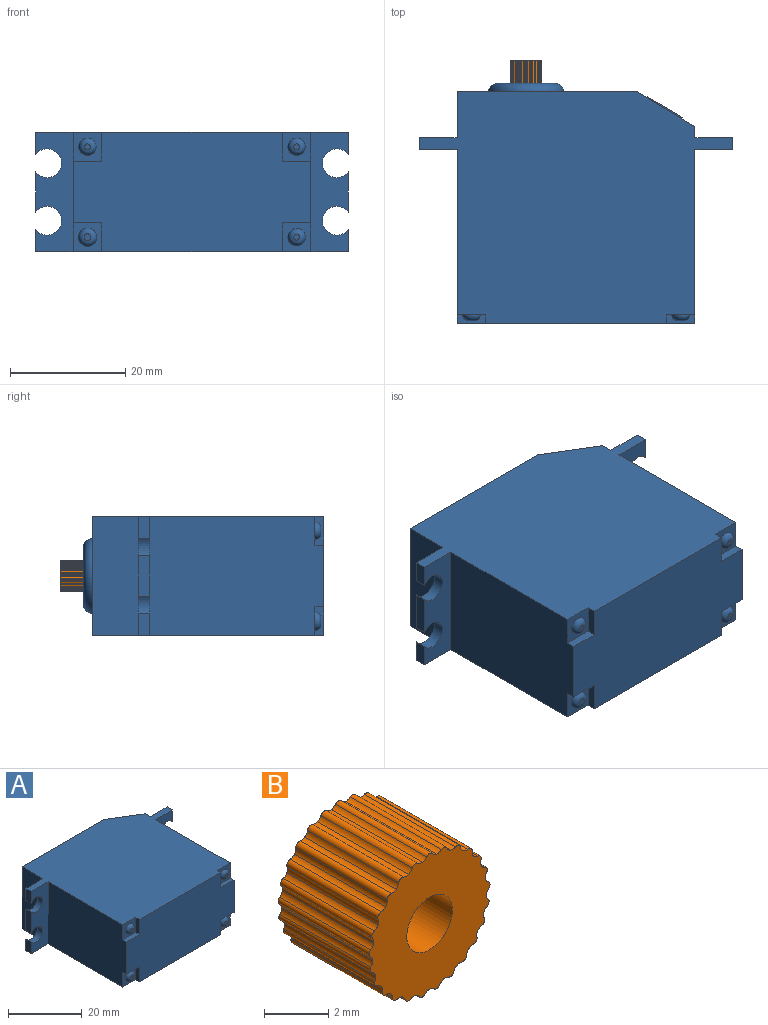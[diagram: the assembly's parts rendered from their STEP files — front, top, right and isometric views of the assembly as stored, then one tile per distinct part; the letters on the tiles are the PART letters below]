
ASSEMBLY  parts=2 mates=1
PART A: 52 faces, bbox 54.3x41.7x20.7 mm
  f0: plane 20.7x10mm, normal (0.51,0.86,0), area 143.4mm2, adj f6,f9,f11,f12,f43,f44,f45,f46
  f1: plane 7x2mm, normal (1,0,0), area 14mm2, adj f34,f35,f39,f42
  f2: plane 7x2mm, normal (-1,0,0), area 14mm2, adj f36,f37,f40,f41
  f3: plane 3.85x2mm, normal (-1,0,0), area 7.7mm2, adj f11,f36,f37,f40
  f4: plane 3.85x2mm, normal (1,0,0), area 7.7mm2, adj f11,f34,f35,f39
  f5: plane 20.7x8mm, normal (-1,0,0), area 165.6mm2, adj f9,f11,f12,f36
  f6: plane 20.7x2mm, normal (1,0,0), area 41.4mm2, adj f0,f9,f11,f35
  f7: plane 41.3x20.7mm, normal (0,-1,0), area 754.9mm2, adj f8,f9,f10,f11,f13,f14,f16,f17
  f8: plane 30.2x20.7mm, normal (-1,0,0), area 610.1mm2, adj f7,f9,f11,f19,f21,f22,f24,f37
  f9: plane 54.3x40.2mm, normal (0,0,1), area 1641.3mm2, adj f0,f5,f6,f7,f8,f10,f12,f16
  f10: plane 30.2x20.7mm, normal (1,0,0), area 610.1mm2, adj f7,f9,f11,f14,f15,f17,f18,f34
  f11: plane 54.3x40.2mm, normal (0,0,-1), area 1641.3mm2, adj f0,f3,f4,f5,f6,f7,f8,f10
  f12: plane 31.3x20.7mm, normal (0,1,0), area 515.2mm2, adj f0,f5,f9,f11,f49
  f13: plane 5x1.5mm, normal (1,0,0), area 7.5mm2, adj f7,f11,f14,f15
  f14: plane 5x1.5mm, normal (0,0,-1), area 7.5mm2, adj f7,f10,f13,f15
  f15: plane 5x5mm, normal (0,-1,0), area 17.9mm2, adj f10,f11,f13,f14,f29
  f16: plane 5x1.5mm, normal (1,0,0), area 7.5mm2, adj f7,f9,f17,f18
  f17: plane 5x1.5mm, normal (0,0,1), area 7.5mm2, adj f7,f10,f16,f18
  f18: plane 5x5mm, normal (0,-1,0), area 17.9mm2, adj f9,f10,f16,f17,f30
  f19: plane 5x1.5mm, normal (0,0,1), area 7.5mm2, adj f7,f8,f20,f21
  f20: plane 5x1.5mm, normal (-1,0,0), area 7.5mm2, adj f7,f9,f19,f21
  f21: plane 5x5mm, normal (0,-1,0), area 17.9mm2, adj f8,f9,f19,f20,f31
  f22: plane 5x1.5mm, normal (0,0,-1), area 7.5mm2, adj f7,f8,f23,f24
  f23: plane 5x1.5mm, normal (-1,0,0), area 7.5mm2, adj f7,f11,f22,f24
  f24: plane 5x5mm, normal (0,-1,0), area 17.1mm2, adj f8,f11,f22,f23,f32
  f25: plane 1.18x1.18mm, normal (0,-1,0), area 1.1mm2, adj f32
  f26: plane 1x1mm, normal (0,-1,0), area 0.8mm2, adj f31
  f27: plane 1x1mm, normal (0,-1,0), area 0.8mm2, adj f30
  f28: plane 1x1mm, normal (0,-1,0), area 0.8mm2, adj f29
  f29: torus R=0.5mm, axis (0,-1,0), area 11.2mm2, adj f15,f28
  f30: torus R=0.5mm, axis (0,-1,0), area 11.2mm2, adj f18,f27
  f31: torus R=0.5mm, axis (0,-1,0), area 11.2mm2, adj f21,f26
  f32: torus R=0.59mm, axis (0,-1,0), area 12.1mm2, adj f24,f25
  f33: plane 3.85x2mm, normal (1,0,0), area 7.7mm2, adj f9,f34,f35,f42
  f34: plane 20.7x6.5mm, normal (0,-1,0), area 97.3mm2, adj f1,f4,f9,f10,f11,f33,f39,f42
  f35: plane 20.7x6.5mm, normal (0,1,0), area 97.3mm2, adj f1,f4,f6,f9,f11,f33,f39,f42
  f36: plane 20.7x6.5mm, normal (0,1,0), area 97.3mm2, adj f2,f3,f5,f9,f11,f38,f40,f41
  f37: plane 20.7x6.5mm, normal (0,-1,0), area 97.3mm2, adj f2,f3,f8,f9,f11,f38,f40,f41
  f38: plane 3.85x2mm, normal (-1,0,0), area 7.7mm2, adj f9,f36,f37,f41
  f39: cylinder r=2.5mm len=5mm, axis (0,1,0), area 25mm2, adj f1,f4,f34,f35
  f40: cylinder r=2.5mm len=5mm, axis (0,1,0), area 25mm2, adj f2,f3,f36,f37
  f41: cylinder r=2.5mm len=5mm, axis (0,1,0), area 25mm2, adj f2,f36,f37,f38
  f42: cylinder r=2.5mm len=5mm, axis (0,1,0), area 25mm2, adj f1,f33,f34,f35
  f43: plane 6.11x3.77mm, normal (0,0,1), area 1.4mm2, adj f0,f44,f46,f47
  f44: plane 14x0.17mm, normal (0.86,-0.51,0), area 2.8mm2, adj f0,f43,f45,f47
  f45: plane 6.11x3.77mm, normal (0,0,-1), area 1.4mm2, adj f0,f44,f46,f47
  f46: plane 14x0.17mm, normal (-0.86,0.51,0), area 2.8mm2, adj f0,f43,f45,f47
  f47: plane 14x6mm, normal (0.51,0.86,0), area 98mm2, adj f43,f44,f45,f46
  f48: plane 10x10mm, normal (0,1,0), area 75.4mm2, adj f49,f50
  f49: torus R=5mm, axis (0,1,0), area 88.2mm2, adj f12,f48
  f50: cylinder r=1mm len=4mm, axis (0,1,0), area 25.1mm2, adj f48,f51
  f51: plane 2x2mm, normal (0,1,0), area 3.1mm2, adj f50
PART B: 78 faces, bbox 5.3x4x5.3 mm
  f0: cylinder r=0.16mm len=4mm, axis (0,-1,0), area 1.2mm2, adj f26,f27,f69,f75
  f1: cylinder r=0.16mm len=4mm, axis (0,-1,0), area 1.2mm2, adj f26,f27,f66,f68
  f2: cylinder r=0.16mm len=4mm, axis (0,-1,0), area 1.2mm2, adj f26,f27,f65,f67
  f3: cylinder r=0.16mm len=4mm, axis (0,-1,0), area 1.2mm2, adj f26,f27,f62,f64
  f4: cylinder r=0.16mm len=4mm, axis (0,-1,0), area 1.2mm2, adj f26,f27,f61,f63
  f5: cylinder r=0.16mm len=4mm, axis (0,-1,0), area 1.2mm2, adj f26,f27,f58,f60
  f6: cylinder r=0.16mm len=4mm, axis (0,-1,0), area 1.2mm2, adj f26,f27,f56,f59
  f7: cylinder r=0.16mm len=4mm, axis (0,-1,0), area 1.2mm2, adj f26,f27,f53,f57
  f8: cylinder r=0.16mm len=4mm, axis (0,-1,0), area 1.2mm2, adj f26,f27,f52,f55
  f9: cylinder r=0.16mm len=4mm, axis (0,-1,0), area 1.2mm2, adj f26,f27,f29,f54
  f10: cylinder r=0.16mm len=4mm, axis (0,-1,0), area 1.2mm2, adj f26,f27,f28,f51
  f11: cylinder r=0.16mm len=4mm, axis (0,-1,0), area 1.2mm2, adj f26,f27,f47,f50
  f12: cylinder r=0.16mm len=4mm, axis (0,-1,0), area 1.2mm2, adj f26,f27,f46,f48
  f13: cylinder r=0.16mm len=4mm, axis (0,-1,0), area 1.2mm2, adj f26,f27,f44,f49
  f14: cylinder r=0.16mm len=4mm, axis (0,-1,0), area 1.2mm2, adj f26,f27,f42,f45
  f15: cylinder r=0.16mm len=4mm, axis (0,-1,0), area 1.2mm2, adj f26,f27,f40,f43
  f16: cylinder r=0.16mm len=4mm, axis (0,-1,0), area 1.2mm2, adj f26,f27,f39,f41
  f17: cylinder r=0.16mm len=4mm, axis (0,-1,0), area 1.2mm2, adj f26,f27,f36,f38
  f18: cylinder r=0.16mm len=4mm, axis (0,-1,0), area 1.2mm2, adj f26,f27,f34,f37
  f19: cylinder r=0.16mm len=4mm, axis (0,-1,0), area 1.2mm2, adj f26,f27,f32,f35
  f20: cylinder r=0.16mm len=4mm, axis (0,-1,0), area 1.2mm2, adj f26,f27,f31,f33
  f21: cylinder r=0.16mm len=4mm, axis (0,-1,0), area 1.2mm2, adj f26,f27,f30,f70
  f22: cylinder r=0.16mm len=4mm, axis (0,-1,0), area 1.2mm2, adj f26,f27,f71,f72
  f23: cylinder r=0.16mm len=4mm, axis (0,-1,0), area 1.2mm2, adj f26,f27,f73,f76
  f24: cylinder r=0.16mm len=4mm, axis (0,-1,0), area 1.2mm2, adj f26,f27,f74,f77
  f25: cylinder r=1mm len=4mm, axis (0,-1,0), area 25.1mm2, adj f26,f27
  f26: plane 5.3x5.29mm, normal (0,1,0), area 17.7mm2, adj f0,f1,f2,f3,f4,f5,f6,f7
  f27: plane 5.3x5.29mm, normal (0,-1,0), area 17.7mm2, adj f0,f1,f2,f3,f4,f5,f6,f7
  f28: cylinder r=0.3mm len=4mm, axis (0,1,0), area 0.9mm2, adj f10,f26,f27,f29
  f29: cylinder r=0.3mm len=4mm, axis (0,1,0), area 0.9mm2, adj f9,f26,f27,f28
  f30: cylinder r=0.3mm len=4mm, axis (0,1,0), area 0.9mm2, adj f21,f26,f27,f31
  f31: cylinder r=0.3mm len=4mm, axis (0,1,0), area 0.9mm2, adj f20,f26,f27,f30
  f32: cylinder r=0.3mm len=4mm, axis (0,1,0), area 0.9mm2, adj f19,f26,f27,f33
  f33: cylinder r=0.3mm len=4mm, axis (0,1,0), area 0.9mm2, adj f20,f26,f27,f32
  f34: cylinder r=0.3mm len=4mm, axis (0,1,0), area 0.9mm2, adj f18,f26,f27,f35
  f35: cylinder r=0.3mm len=4mm, axis (0,1,0), area 0.9mm2, adj f19,f26,f27,f34
  f36: cylinder r=0.3mm len=4mm, axis (0,1,0), area 0.9mm2, adj f17,f26,f27,f37
  f37: cylinder r=0.3mm len=4mm, axis (0,1,0), area 0.9mm2, adj f18,f26,f27,f36
  f38: cylinder r=0.3mm len=4mm, axis (0,1,0), area 0.9mm2, adj f17,f26,f27,f39
  f39: cylinder r=0.3mm len=4mm, axis (0,1,0), area 0.9mm2, adj f16,f26,f27,f38
  f40: cylinder r=0.3mm len=4mm, axis (0,1,0), area 0.9mm2, adj f15,f26,f27,f41
  f41: cylinder r=0.3mm len=4mm, axis (0,1,0), area 0.9mm2, adj f16,f26,f27,f40
  f42: cylinder r=0.3mm len=4mm, axis (0,1,0), area 0.9mm2, adj f14,f26,f27,f43
  f43: cylinder r=0.3mm len=4mm, axis (0,1,0), area 0.9mm2, adj f15,f26,f27,f42
  f44: cylinder r=0.3mm len=4mm, axis (0,1,0), area 0.9mm2, adj f13,f26,f27,f45
  f45: cylinder r=0.3mm len=4mm, axis (0,1,0), area 0.9mm2, adj f14,f26,f27,f44
  f46: cylinder r=0.3mm len=4mm, axis (0,1,0), area 0.9mm2, adj f12,f26,f27,f47
  f47: cylinder r=0.3mm len=4mm, axis (0,1,0), area 0.9mm2, adj f11,f26,f27,f46
  f48: cylinder r=0.3mm len=4mm, axis (0,1,0), area 0.9mm2, adj f12,f26,f27,f49
  f49: cylinder r=0.3mm len=4mm, axis (0,1,0), area 0.9mm2, adj f13,f26,f27,f48
  f50: cylinder r=0.3mm len=4mm, axis (0,1,0), area 0.9mm2, adj f11,f26,f27,f51
  f51: cylinder r=0.3mm len=4mm, axis (0,1,0), area 0.9mm2, adj f10,f26,f27,f50
  f52: cylinder r=0.3mm len=4mm, axis (0,1,0), area 0.9mm2, adj f8,f26,f27,f53
  f53: cylinder r=0.3mm len=4mm, axis (0,1,0), area 0.9mm2, adj f7,f26,f27,f52
  f54: cylinder r=0.3mm len=4mm, axis (0,1,0), area 0.9mm2, adj f9,f26,f27,f55
  f55: cylinder r=0.3mm len=4mm, axis (0,1,0), area 0.9mm2, adj f8,f26,f27,f54
  f56: cylinder r=0.3mm len=4mm, axis (0,1,0), area 0.9mm2, adj f6,f26,f27,f57
  f57: cylinder r=0.3mm len=4mm, axis (0,1,0), area 0.9mm2, adj f7,f26,f27,f56
  f58: cylinder r=0.3mm len=4mm, axis (0,1,0), area 0.9mm2, adj f5,f26,f27,f59
  f59: cylinder r=0.3mm len=4mm, axis (0,1,0), area 0.9mm2, adj f6,f26,f27,f58
  f60: cylinder r=0.3mm len=4mm, axis (0,1,0), area 0.9mm2, adj f5,f26,f27,f61
  f61: cylinder r=0.3mm len=4mm, axis (0,1,0), area 0.9mm2, adj f4,f26,f27,f60
  f62: cylinder r=0.3mm len=4mm, axis (0,1,0), area 0.9mm2, adj f3,f26,f27,f63
  f63: cylinder r=0.3mm len=4mm, axis (0,1,0), area 0.9mm2, adj f4,f26,f27,f62
  f64: cylinder r=0.3mm len=4mm, axis (0,1,0), area 0.9mm2, adj f3,f26,f27,f65
  f65: cylinder r=0.3mm len=4mm, axis (0,1,0), area 0.9mm2, adj f2,f26,f27,f64
  f66: cylinder r=0.3mm len=4mm, axis (0,1,0), area 0.9mm2, adj f1,f26,f27,f67
  f67: cylinder r=0.3mm len=4mm, axis (0,1,0), area 0.9mm2, adj f2,f26,f27,f66
  f68: cylinder r=0.3mm len=4mm, axis (0,1,0), area 0.9mm2, adj f1,f26,f27,f69
  f69: cylinder r=0.3mm len=4mm, axis (0,1,0), area 0.9mm2, adj f0,f26,f27,f68
  f70: cylinder r=0.3mm len=4mm, axis (0,1,0), area 0.9mm2, adj f21,f26,f27,f71
  f71: cylinder r=0.3mm len=4mm, axis (0,1,0), area 0.9mm2, adj f22,f26,f27,f70
  f72: cylinder r=0.3mm len=4mm, axis (0,1,0), area 0.9mm2, adj f22,f26,f27,f73
  f73: cylinder r=0.3mm len=4mm, axis (0,1,0), area 0.9mm2, adj f23,f26,f27,f72
  f74: cylinder r=0.3mm len=4mm, axis (0,1,0), area 0.9mm2, adj f24,f26,f27,f75
  f75: cylinder r=0.3mm len=4mm, axis (0,1,0), area 0.9mm2, adj f0,f26,f27,f74
  f76: cylinder r=0.3mm len=4mm, axis (0,1,0), area 0.9mm2, adj f23,f26,f27,f77
  f77: cylinder r=0.3mm len=4mm, axis (0,1,0), area 0.9mm2, adj f24,f26,f27,f76
PLACE A at identity fixed
PLACE B t=(-4.68,41.7,0.86)mm
MATE revolute A.f49 <-> B.f25  axis (0,1,0) through (-4.68,41.7,0.86)mm
